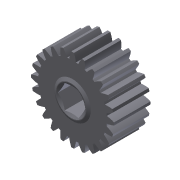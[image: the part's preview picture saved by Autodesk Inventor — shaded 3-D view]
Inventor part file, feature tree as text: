
AUTODESK INVENTOR PART (.ipt)
format: ipt  version: 2011 (Build 150239000, 239)  size: 269,312 bytes
history: native  units: mm (DEFAULTED — no unit token found)
features: sketch x5, other x4, extrude x3, plane x3, chamfer x1, revolve x1, projected_geometry x1
ambient origin geometry x8: Origin, YZ Plane, XZ Plane, XY Plane, X Axis, Y Axis, Z Axis, Center Point
bodies: Solid1 (feature_tree)
feature tree (18):
  other  "Gear 24T 20dp 375hex"
  extrude  "Extrusion1"  Depth=14.605mm TaperAngle=0.0deg
  plane  "Work Plane1"
  plane  "Work Plane2"
  plane  "Work Plane3"
  other  "Spur Gear"
  extrude  "Extrusion2"  Depth=76.2mm TaperAngle=0.0deg
  extrude  "Extrusion3"  TaperAngle=0.0deg  [1 undecoded]
  chamfer  "Chamfer1"  Distance=46.99mm
  revolve  "Revolution1"  [1 undecoded]
  sketch  "Sketch1"  dims[d0=33.3248mm d1=14.605mm d2=0.0mm]
  sketch  "Sketch2"  dims[d3=30.48mm d4=76.2mm d5=0.0mm]
  other  "Srf1"
  sketch  "Sketch3"  dims[d6=0.0mm d7=1.308997mm d9=0.0mm d14=0.0mm d15=46.99mm]
  sketch  "Sketch4"  dims[d16=0.0mm d17=0.0mm d18=0.0mm d19=46.99mm]
  sketch  "Sketch5"  dims[d20=14.605mm d21=0.635mm d22=0.0mm d23=9.525mm d24=0.635mm d25=0.0mm d26=1.143mm d27=3.175mm d28=26.345745mm d29=1.143mm d30=90.0deg]
  other  "Pitch Diameter"
  projected_geometry  "Project Cut Edges1"
note: 2 required parameter values undecoded (feature->parameter linkage not recoverable at this tier; creation-order binding heuristic only, values carry confidence <= 0.55)